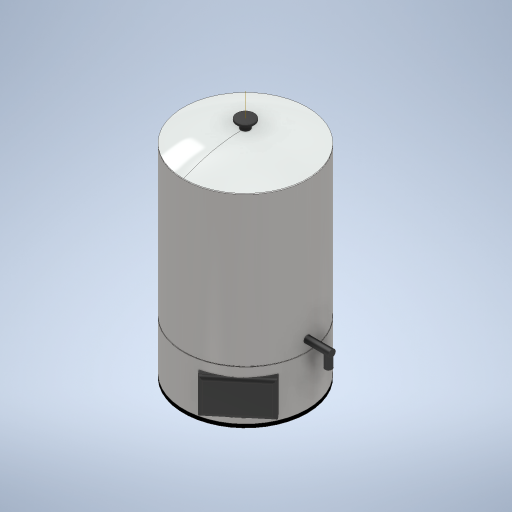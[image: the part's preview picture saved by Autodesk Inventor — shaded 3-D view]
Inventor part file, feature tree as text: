
AUTODESK INVENTOR PART (.ipt)
format: ipt  version: 2024 (Build 280153000, 153)  size: 414,720 bytes
history: native  units: mm
features: sketch x11, extrude x10, plane x4, fillet x3, revolve x1, chamfer x1, projected_geometry x1, other x1
ambient origin geometry x8: Origin, YZ Plane, XZ Plane, XY Plane, X Axis, Y Axis, Z Axis, Center Point
bodies: Solid1 (feature_tree)
feature tree (32):
  extrude  "Extrusion1"  Depth=2.0mm TaperAngle=0.0deg
  extrude  "Extrusion2"  Depth=420.0mm TaperAngle=0.0deg
  fillet  "Fillet2"  Radius=1.0mm
  extrude  "Extrusion5"  Depth=140.0mm TaperAngle=0.0deg
  fillet  "Fillet3"  Radius=1.0mm
  extrude  "Extrusion6"  Depth=10.0mm
  revolve  "Revolution1"  Angle=360.0deg
  plane  "Work Plane1"
  extrude  "Extrusion8"  Depth=25.0mm
  extrude  "Extrusion9"  Depth=10.0mm
  chamfer  "Chamfer1"  Distance=15.0mm
  plane  "Work Plane2"
  extrude  "Extrusion10"  Depth=10.0mm
  plane  "Work Plane4"
  extrude  "Extrusion11"  Depth=70.0mm TaperAngle=0.0deg
  extrude  "Extrusion12"  Depth=10.0mm TaperAngle=0.0deg
  plane  "Work Plane8"
  extrude  "Extrusion13"  Depth=10.0mm
  fillet  "Fillet4"  Radius=100.0mm
  sketch  "Sketch1"  dims[d0=350.0mm d1=2.0mm d2=0.0mm]
  sketch  "Sketch2"  dims[d3=349.0mm d4=420.0mm d5=0.0mm d12=1.0mm]
  sketch  "Sketch5"  dims[d13=349.0mm d14=140.0mm d15=0.0mm d16=1.0mm]
  sketch  "Sketch6"  dims[d17=10.0mm d18=0.0mm d22=3.0mm]
  sketch  "Sketch9"  dims[d24=3.0mm d25=360.0deg]
  sketch  "Sketch10"  dims[d26=39.0mm d27=25.0mm]
  sketch  "Sketch11"  dims[d28=10.0mm d29=0.0mm d30=50.0mm d31=15.0mm d32=0.0mm]
  sketch  "Sketch12"  dims[d33=10.0mm d34=2.0mm d35=45.0deg d36=32.0mm]
  sketch  "Sketch13"  dims[d37=20.0mm d38=70.0mm d39=0.0mm]
  sketch  "Sketch14"  dims[d40=20.0mm d41=10.0mm d42=0.0mm]
  projected_geometry  "Projected Loop1"
  other  "Work Axis1"
  sketch  "Sketch15"  dims[d43=30.0mm d44=0.0mm d45=22.68928mm d49=100.0mm d50=160.0mm d51=75.0mm d52=180.0mm d53=0.0mm d54=10.0mm]
